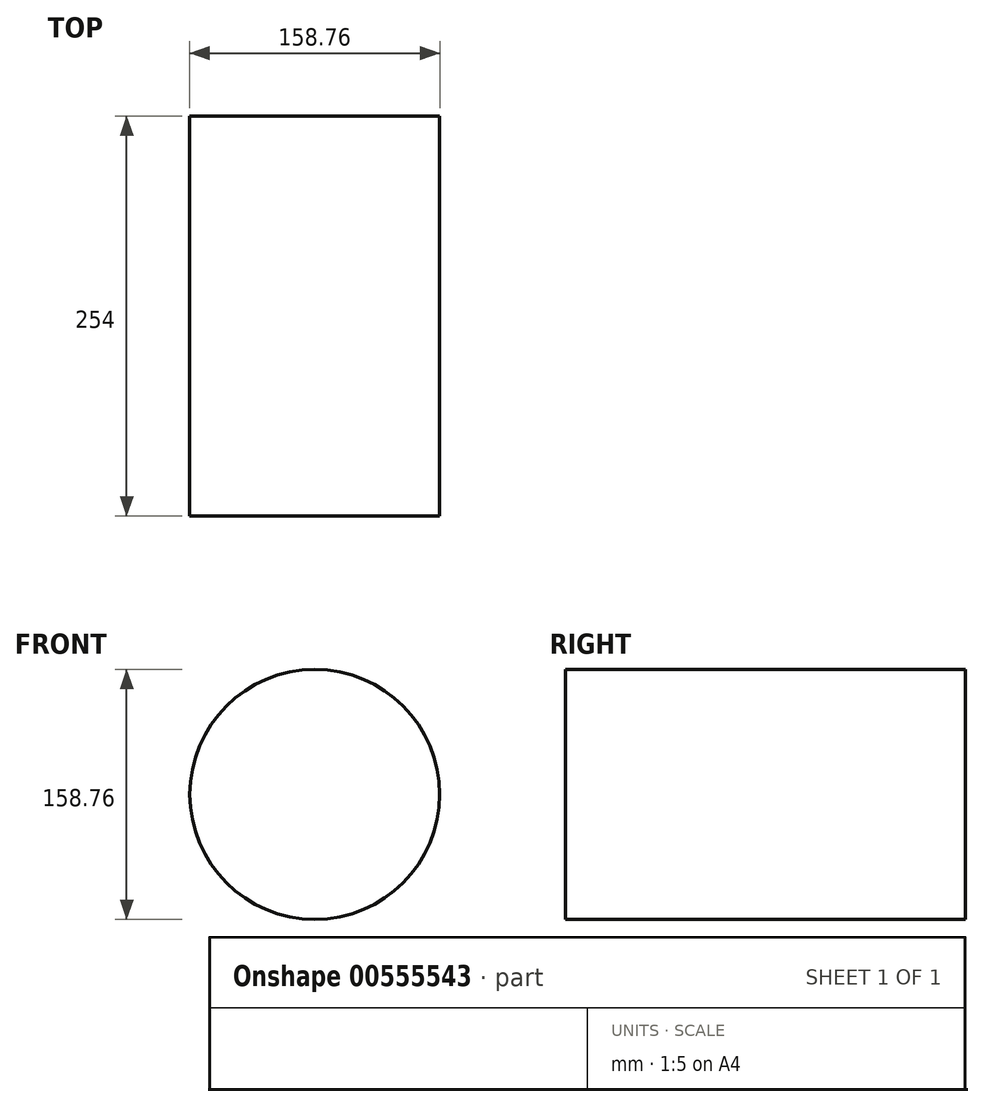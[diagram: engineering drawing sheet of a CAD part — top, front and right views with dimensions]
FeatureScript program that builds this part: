
annotation { "Feature Type Name" : "Feature", "Feature Type Description" : "" }
export const myFeature = defineFeature(function(context is Context, id is Id, definition is map)
    precondition{}
    {
        {
            var Q0;
            Q0=qCreatedBy(makeId("Front.planeOp"),FACE);
            var sketch = newSketch(context, id + "F0", { "sketchPlane" : qUnion([Q0])});
            skCircle(sketch, "E0", {"center": v(0, 0) * mm, "radius": 79.38 * mm});
            skSolve(sketch);
        }
        {
            var Q0;
            Q0 = qSketchRegion(id + "F0", true);
            extrude(context, id + "F1", {"entities" : qUnion([Q0]), "depth" : 254 * mm, "offsetDistance" : 25.4 * mm});
        }
    });
